# Revit family: Lighting-Linear_Recessed-Philips_Ledalite-TruGroove_Micro-Corner
name_source: partatom
category: Lighting Fixtures
revit_build: Autodesk Revit 2017 (Build: 20160720_1515(x64)
units: mm (PartAtom-declared; Revit-internal decimal feet)

## family parameters
Cut with Voids When Loaded = No
Host = Face
Light Source = No
OmniClass Number = 23.80.70.11.14.17
OmniClass Title = Direct/Indirect
Part Type = Normal
Room Calculation Point = No
Round Connector Dimension = Use Diameter
Shared = No

## types (2) — shared parameters
Apparent Load = 0 VA
Available Finishes = White
C Length = 2' - 1 13/128"
Default Elevation = 0' - 0"
Driver = Consult your Signify representative for other supported drivers.
Frequency = 60 Hz
Height = 0' - 3 17/32"
Housing = Standard
Housing Material Finish = Aluminum-Signify-Powder-Coated-White
Lamp = -
Last Updated = 9.17.18
Length = 2' - 1 13/128"
Lens Material Finish = Acrylic-Signify-Lens
Manufacturer = Ledalite
Number of Poles = 1
Phase = 1
Power Factor = 1
Product Documentation Link = Contact Signify for Product Documentation
Product Family = TruGroove Recessed Micro-Corner
Product Page URL = http://www.lightingproducts.philips.com
URL = https://www.signify.com
Version = 2017 v1.0b
Voltage = 0 V
Wattage Comments = -
Width = 0' - 1 3/4"
Wiring Type = Contact Signify for a complete list of available options.
eCatalog URL = www.ledalite.com

## per-type parameters (varying)
| type | Catalog Number | Description | Drywall | Grid | Inset | Model | Mounting Method |
| Corner - Drywall Housing | TruGroove Recessed Micro Corner - Drywall Housing | TruGroove Recessed Micro Corner - Drywall Housing | Yes | No | 0' - 0 17/128" | TruGroove Recessed Micro Corner - Drywall Housing | Drywall |
| Corner - T-Grid Housing | TruGroove Recessed Micro Corner - T-GridHousing | TruGroove Recessed Micro Corner - T-GridHousing | No | Yes | 0' - 0 25/128" | TruGroove Recessed Micro Corner - T-GridHousing | T-Grid |

## geometry (parser evidence)
native form markers: Sweep x6
no freeform markers — native parametric forms only
